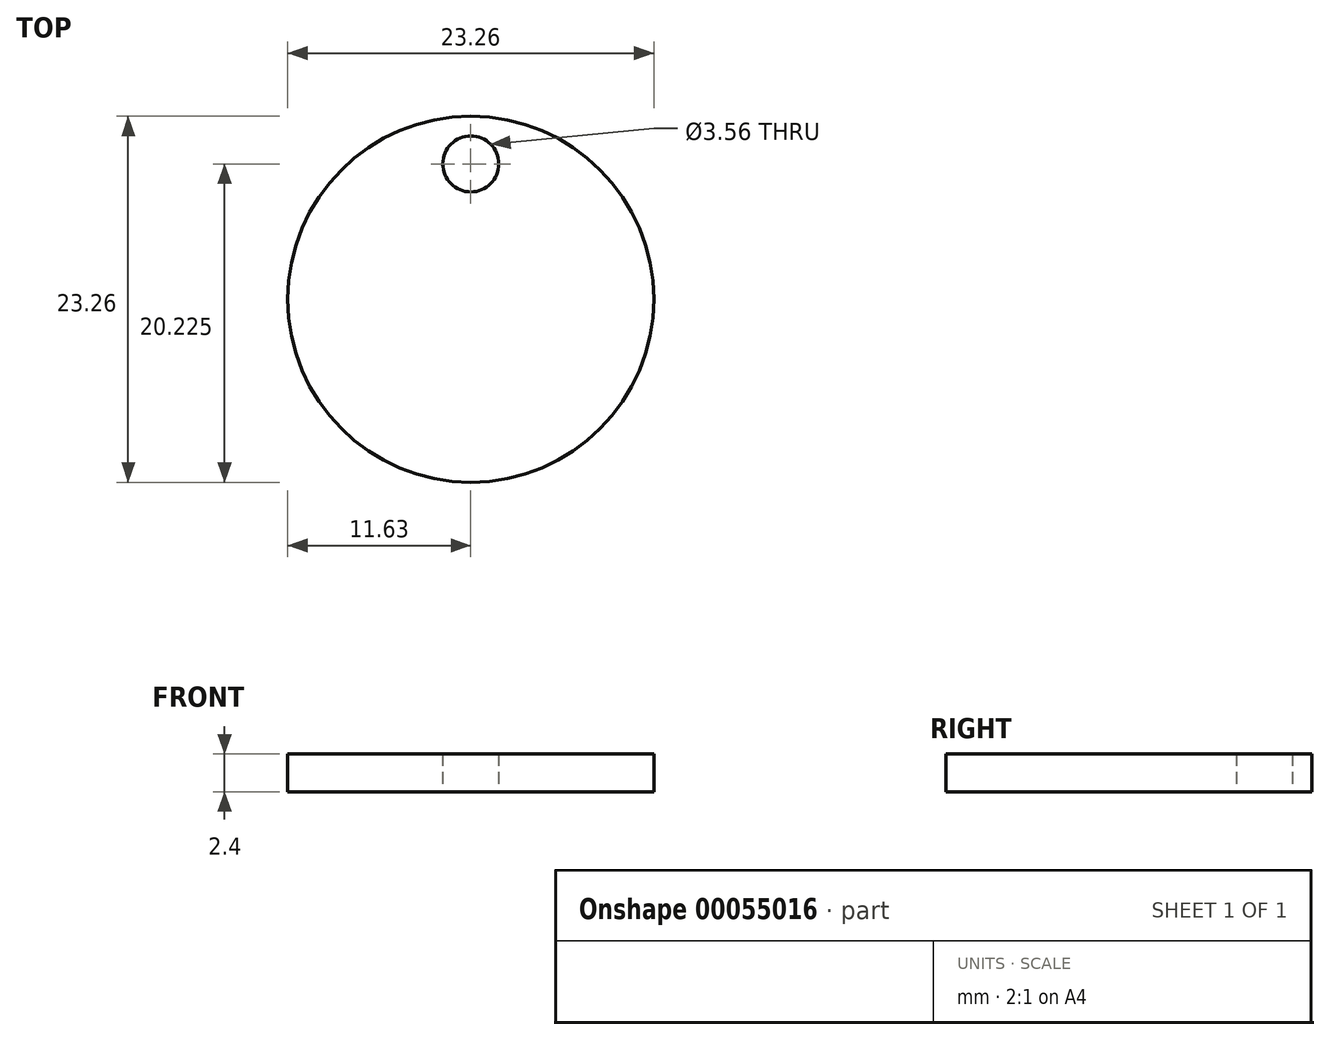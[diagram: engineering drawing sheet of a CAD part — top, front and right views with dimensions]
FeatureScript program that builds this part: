
annotation { "Feature Type Name" : "Feature", "Feature Type Description" : "" }
export const myFeature = defineFeature(function(context is Context, id is Id, definition is map)
    precondition{}
    {
        {
            var Q0;
            Q0=qCreatedBy(makeId("Top.planeOp"),FACE);
            var sketch = newSketch(context, id + "F0", { "sketchPlane" : qUnion([Q0])});
            skCircle(sketch, "E0", {"center": v(0, 0) * mm, "radius": 11.62 * mm});
            skCircle(sketch, "E1", {"center": v(0, 8.6) * mm, "radius": 1.78 * mm});
            skSolve(sketch);
        }
        {
            var Q0;
            Q0=makeQuery(id+"F0.imprint","IMPRINT",FACE,{"disambiguationData":[TD([[makeQuery(id+"F0.imprint","IMPRINT",EDGE,{"derivedFrom":sQuery(id+"F0.wireOp",EDGE,"E0")}),1.0]])]});
            extrude(context, id + "F1", {"entities" : qUnion([Q0]), "depth" : 2.4 * mm});
        }
    });
